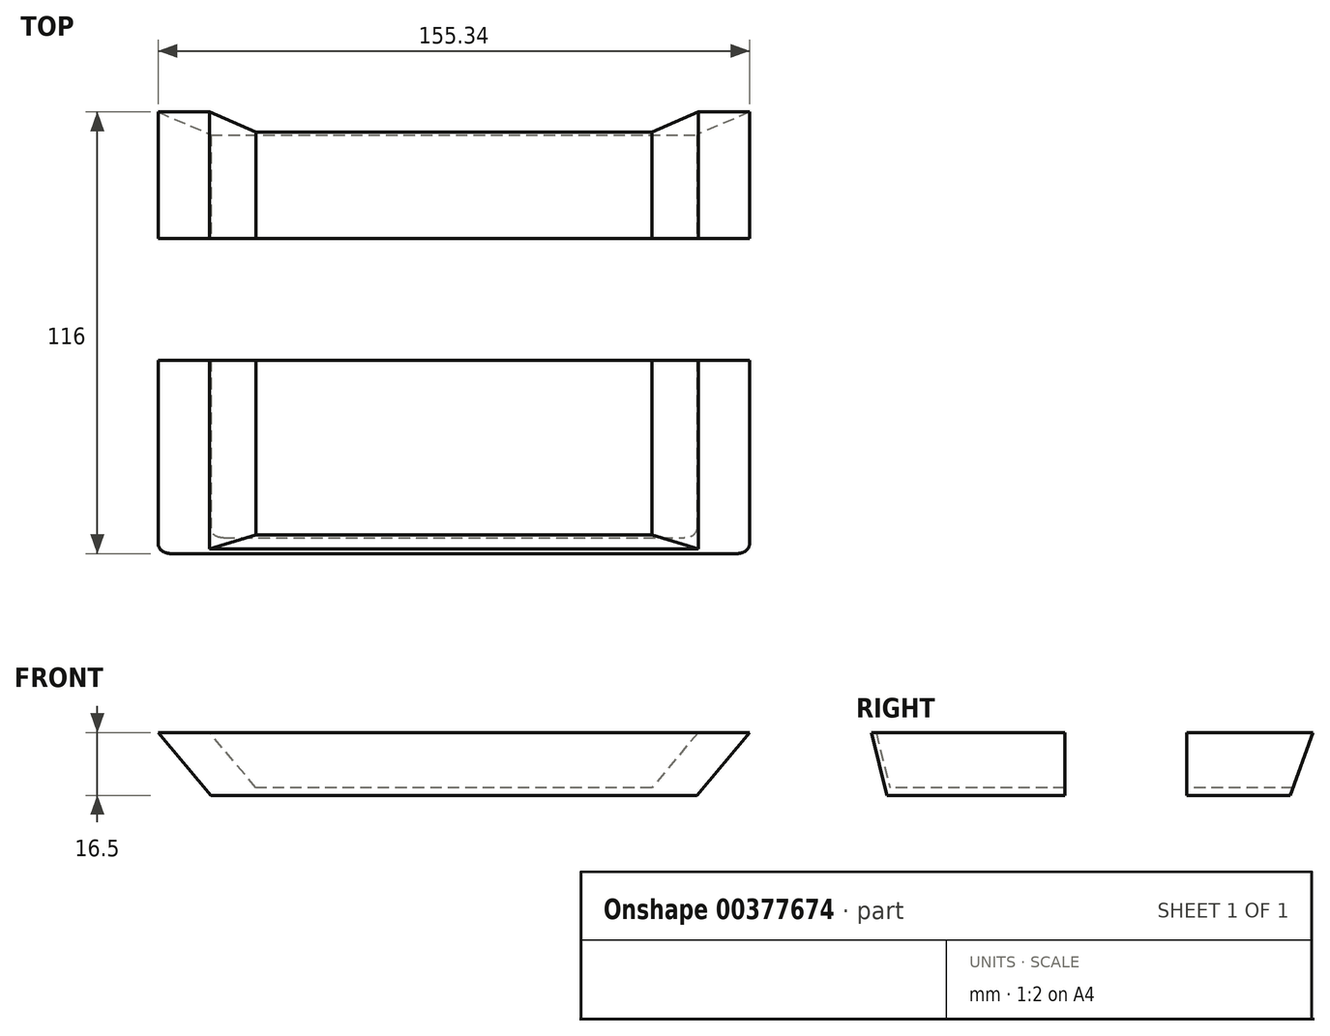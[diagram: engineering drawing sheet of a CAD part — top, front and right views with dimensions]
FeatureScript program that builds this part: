
annotation { "Feature Type Name" : "Feature", "Feature Type Description" : "" }
export const myFeature = defineFeature(function(context is Context, id is Id, definition is map)
    precondition{}
    {
        {
            var Q0;
            Q0=qCreatedBy(makeId("Front.planeOp"),FACE);
            var sketch = newSketch(context, id + "F0", { "sketchPlane" : qUnion([Q0])});
            skLineSegment(sketch, "E0", {"start": v(0, 0) * mm, "end": v(97.37, 0) * mm});
            skLineSegment(sketch, "E1", {"start": v(0, 0) * mm, "end": v(12.17, 14.5) * mm});
            skLineSegment(sketch, "E2", {"start": v(12.17, 14.5) * mm, "end": v(25.67, 14.5) * mm});
            skLineSegment(sketch, "E3", {"start": v(25.67, 14.5) * mm, "end": v(11.82, -2) * mm});
            skLineSegment(sketch, "E4", {"start": v(-52, 0) * mm, "end": v(-52, 76) * mm, "construction": true});
            skLineSegment(sketch, "E5.MirrorCS", {"start": v(-104, 0) * mm, "end": v(-116.17, 14.5) * mm});
            skLineSegment(sketch, "E6.MirrorCS", {"start": v(-116.17, 14.5) * mm, "end": v(-129.67, 14.5) * mm});
            skLineSegment(sketch, "E7.MirrorCS", {"start": v(-129.67, 14.5) * mm, "end": v(-115.82, -2) * mm});
            skLineSegment(sketch, "E8.MirrorCS", {"start": v(-104, 0) * mm, "end": v(-201.37, 0) * mm});
            skLineSegment(sketch, "E9", {"start": v(-115.82, -2) * mm, "end": v(11.82, -2) * mm});
            skLineSegment(sketch, "E10", {"start": v(-104, 0) * mm, "end": v(0, 0) * mm});
            skPoint(sketch, "E11.start.orphan", {"position": v(-117.5, 0) * mm});
            skPoint(sketch, "E12.end.orphan", {"position": v(13.5, 0) * mm});
            skPoint(sketch, "E12.start.orphan", {"position": v(13.5, -2) * mm});
            skSolve(sketch);
        }
        {
            var Q0;
            {var subQ0=sQuery(id+"F0.wireOp",EDGE,"E1");Q0=makeQuery(id+"F0.imprint","IMPRINT",FACE,{"disambiguationData":[TD([[makeQuery(id+"F0.imprint","IMPRINT",EDGE,{"derivedFrom":subQ0}),-1.0]])]});}
            var Q1;
            Q1=makeQuery(id+"F0.imprint","IMPRINT",FACE,{"disambiguationData":[TD([[makeQuery(id+"F0.imprint","IMPRINT",EDGE,{"derivedFrom":sQuery(id+"F0.wireOp",EDGE,"E6.MirrorCS")}),1.0]])]});
            var Q2;
            {var subQ0=sQuery(id+"F0.wireOp",EDGE,"E11");Q2=makeQuery(id+"F0.imprint","IMPRINT",FACE,{"disambiguationData":[TD([[makeQuery(id+"F0.imprint","IMPRINT",EDGE,{"derivedFrom":subQ0}),1.0]])]});}
            var Q3;
            {var subQ4=sQuery(id+"F0.wireOp",EDGE,"E9");Q3=makeQuery(id+"F0.imprint","IMPRINT",FACE,{"disambiguationData":[TD([[makeQuery(id+"F0.imprint","IMPRINT",EDGE,{"derivedFrom":subQ4}),1.0]])]});}
            extrude(context, id + "F1", {"entities" : qUnion([Q0, Q1, Q2, Q3]), "oppositeDirection" : true, "depth" : 116 * mm, "offsetDistance" : 25 * mm});
        }
        {
            var Q0;
            Q0=qCreatedBy(makeId("Right.planeOp"),FACE);
            var sketch = newSketch(context, id + "F2", { "sketchPlane" : qUnion([Q0])});
            skLineSegment(sketch, "E13.0", {"start": v(116, 14.5) * mm, "end": v(0, 14.5) * mm, "construction": true});
            skLineSegment(sketch, "E14.0", {"start": v(0, 14.5) * mm, "end": v(0, -2) * mm});
            skLineSegment(sketch, "E15", {"start": v(0, 14.5) * mm, "end": v(4.11, -2) * mm});
            skLineSegment(sketch, "E16", {"start": v(0, 14.06) * mm, "end": v(0, -2) * mm});
            skLineSegment(sketch, "E17", {"start": v(4.11, -2) * mm, "end": v(0, -2) * mm});
            skLineSegment(sketch, "E18", {"start": v(5.35, -2) * mm, "end": v(1.24, 14.5) * mm});
            skLineSegment(sketch, "E19", {"start": v(0, 14.5) * mm, "end": v(1.24, 14.5) * mm});
            skLineSegment(sketch, "E20", {"start": v(4.11, -2) * mm, "end": v(5.35, -2) * mm});
            skLineSegment(sketch, "E21", {"start": v(50.8, -2) * mm, "end": v(50.8, 14.5) * mm});
            skLineSegment(sketch, "E22", {"start": v(50.8, 14.5) * mm, "end": v(82.8, 14.5) * mm});
            skLineSegment(sketch, "E23", {"start": v(82.8, 14.5) * mm, "end": v(82.8, -2) * mm});
            skLineSegment(sketch, "E24", {"start": v(82.8, -2) * mm, "end": v(50.8, -2) * mm});
            skLineSegment(sketch, "E25", {"start": v(116, 14.5) * mm, "end": v(116, -2) * mm});
            skLineSegment(sketch, "E26", {"start": v(116, -2) * mm, "end": v(110, -2) * mm});
            skLineSegment(sketch, "E27", {"start": v(110, -2) * mm, "end": v(116, 14.5) * mm});
            skSolve(sketch);
        }
        {
            var Q0;
            Q0=makeQuery(id+"F2.imprint","IMPRINT",FACE,{"disambiguationData":[TD([[makeQuery(id+"F2.imprint","IMPRINT",EDGE,{"derivedFrom":sQuery(id+"F2.wireOp",EDGE,"E14.0")}),1.0]])]});
            var Q1;
            Q1=makeQuery(id+"F2.imprint","IMPRINT",FACE,{"disambiguationData":[TD([[makeQuery(id+"F2.imprint","IMPRINT",EDGE,{"derivedFrom":sQuery(id+"F2.wireOp",EDGE,"E21")}),-1.0]])]});
            var Q2;
            Q2=makeQuery(id+"F2.imprint","IMPRINT",FACE,{"disambiguationData":[TD([[makeQuery(id+"F2.imprint","IMPRINT",EDGE,{"derivedFrom":sQuery(id+"F2.wireOp",EDGE,"E25")}),-1.0]])]});
            extrude(context, id + "F3", {"entities" : qUnion([Q0, Q1, Q2]), "operationType" : NewBodyOperationType.REMOVE, "endBound" : BoundingType.THROUGH_ALL, "oppositeDirection" : true, "depth" : 25 * mm, "offsetDistance" : 25 * mm, "hasSecondDirection" : true, "secondDirectionBound" : SecondDirectionBoundingType.THROUGH_ALL, "secondDirectionOppositeDirection" : false, "secondDirectionDepth" : 25 * mm});
        }
        {
            var Q0;
            Q0=makeQuery(id+"F2.imprint","IMPRINT",FACE,{"disambiguationData":[TD([[makeQuery(id+"F2.imprint","IMPRINT",EDGE,{"derivedFrom":sQuery(id+"F2.wireOp",EDGE,"E15")}),1.0]])]});
            var Q1;
            Q1=makeQuery(id+"F1.opExtrude","SWEPT_FACE",FACE,{"disambiguationData":[OSD([sQuery(id+"F0.wireOp",EDGE,"E3")])]});
            var Q2;
            Q2=makeQuery(id+"F1.opExtrude","SWEPT_FACE",FACE,{"disambiguationData":[OSD([sQuery(id+"F0.wireOp",EDGE,"E5.MirrorCS")])]});
            extrude(context, id + "F4", {"entities" : qUnion([Q0]), "operationType" : NewBodyOperationType.ADD, "endBound" : BoundingType.UP_TO_SURFACE, "depth" : 25 * mm, "endBoundEntityFace" : qUnion([Q1]), "offsetDistance" : 25 * mm, "hasSecondDirection" : true, "secondDirectionBound" : SecondDirectionBoundingType.UP_TO_SURFACE, "secondDirectionOppositeDirection" : true, "secondDirectionDepth" : 25 * mm, "secondDirectionBoundEntityFace" : qUnion([Q2])});
        }
        {
            var Q0;
            Q0=makeQuery(id+"F3.boolean.opBoolean","INTERSECT",EDGE,{"derivedFrom":[makeQuery(id+"F1.opExtrude","SWEPT_FACE",FACE,{"disambiguationData":[OSD([sQuery(id+"F0.wireOp",EDGE,"E3")])]}),makeQuery(id+"F3.opExtrude","SWEPT_FACE",FACE,{"disambiguationData":[OSD([sQuery(id+"F2.wireOp",EDGE,"E15")])]})]});
            var Q1;
            Q1=makeQuery(id+"F3.boolean.opBoolean","INTERSECT",EDGE,{"derivedFrom":[makeQuery(id+"F1.opExtrude","SWEPT_FACE",FACE,{"disambiguationData":[OSD([sQuery(id+"F0.wireOp",EDGE,"E7.MirrorCS")])]}),makeQuery(id+"F3.opExtrude","SWEPT_FACE",FACE,{"disambiguationData":[OSD([sQuery(id+"F2.wireOp",EDGE,"E15")])]})]});
            fillet(context, id + "F5", {"entities" : qUnion([Q0, Q1]), "radius" : 3 * mm, "tangentPropagation" : true, "allowEdgeOverflow" : false});
        }
    });
